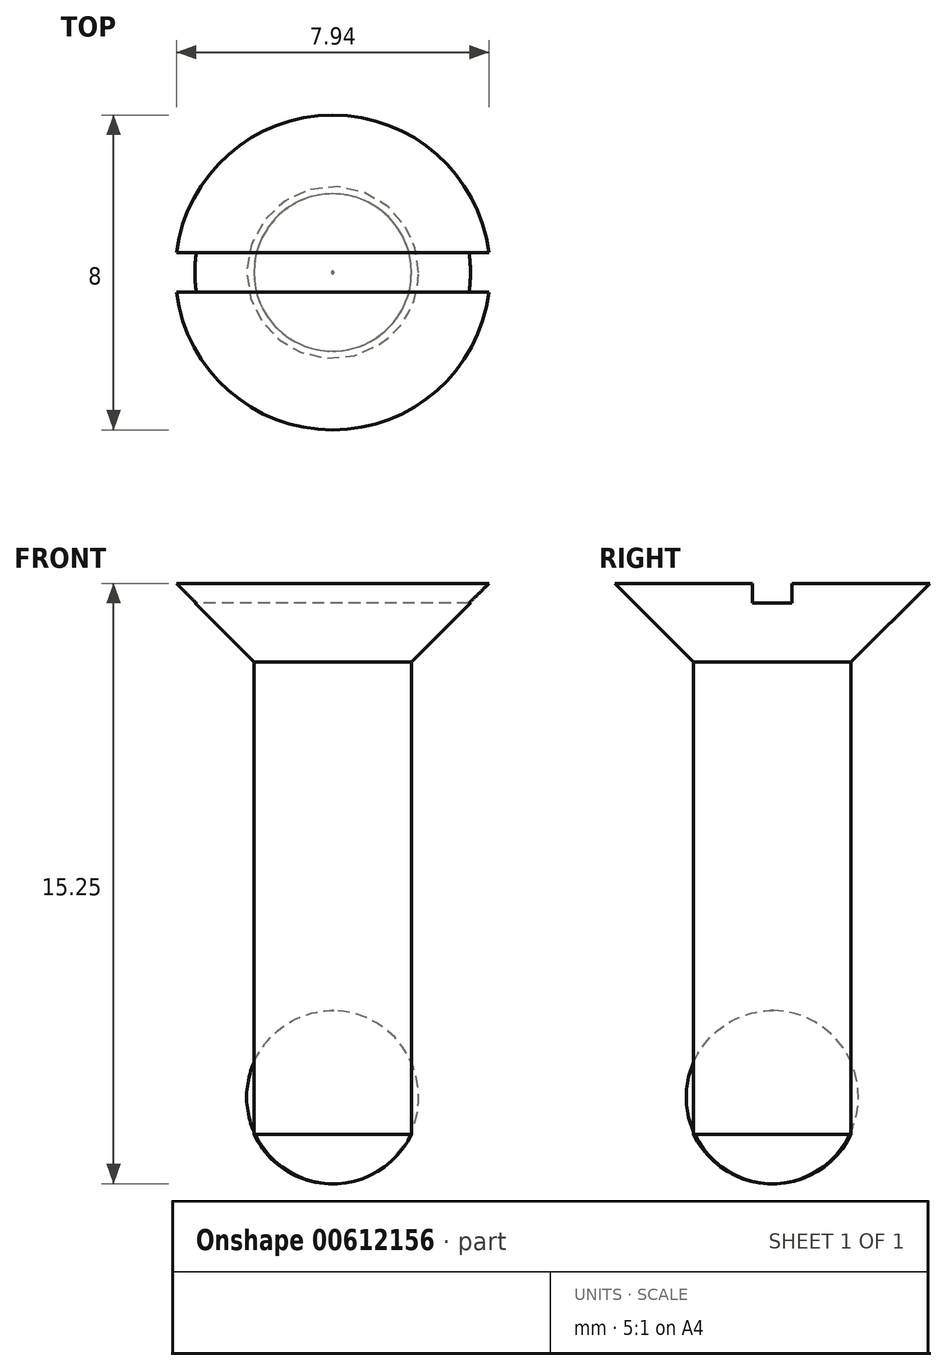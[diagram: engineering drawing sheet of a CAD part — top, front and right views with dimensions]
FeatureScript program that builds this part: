
annotation { "Feature Type Name" : "Feature", "Feature Type Description" : "" }
export const myFeature = defineFeature(function(context is Context, id is Id, definition is map)
    precondition{}
    {
        {
            var Q0;
            Q0=qCreatedBy(makeId("Front.planeOp"),FACE);
            var sketch = newSketch(context, id + "F0", { "sketchPlane" : qUnion([Q0])});
            skLineSegment(sketch, "E0", {"start": v(0, 0) * mm, "end": v(0, 14) * mm});
            skLineSegment(sketch, "E1", {"start": v(0, 14) * mm, "end": v(4, 14) * mm});
            skLineSegment(sketch, "E2", {"start": v(4, 14) * mm, "end": v(2, 12) * mm});
            skLineSegment(sketch, "E3", {"start": v(2, 12) * mm, "end": v(2, 0) * mm});
            skArc(sketch, "E4", {"start": v(0, -1.25) * mm, "mid": v(1.18, -0.92) * mm, "end": v(2, 0) * mm});
            skLineSegment(sketch, "E5", {"start": v(0, -1.25) * mm, "end": v(0, 0) * mm});
            skSolve(sketch);
        }
        {
            var Q0;
            Q0=makeQuery(id+"F0.imprint","IMPRINT",FACE,{"disambiguationData":[TD([[makeQuery(id+"F0.imprint","IMPRINT",EDGE,{"derivedFrom":sQuery(id+"F0.wireOp",EDGE,"E0")}),-1.0]])]});
            var Q1;
            Q1=sQuery(id+"F0.wireOp",EDGE,"E0");
            revolve(context, id + "F1", {"entities" : qUnion([Q0]), "axis" : qUnion([Q1]), "revolveType" : RevolveType.FULL});
        }
        {
            var Q0;
            Q0=makeQuery(id+"F1.opRevolve","SWEPT_FACE",FACE,{"disambiguationData":[OSD([sQuery(id+"F0.wireOp",EDGE,"E1")])]});
            var sketch = newSketch(context, id + "F2", { "sketchPlane" : qUnion([Q0])});
            skLineSegment(sketch, "E6.bottom", {"start": v(5.06, -0.5) * mm, "end": v(-5.06, -0.5) * mm});
            skLineSegment(sketch, "E6.top", {"start": v(5.06, 0.5) * mm, "end": v(-5.06, 0.5) * mm});
            skLineSegment(sketch, "E6.left", {"start": v(5.06, -0.5) * mm, "end": v(5.06, 0.5) * mm});
            skLineSegment(sketch, "E6.right", {"start": v(-5.06, -0.5) * mm, "end": v(-5.06, 0.5) * mm});
            skPoint(sketch, "E6.middle", {"position": v(0, 0) * mm});
            skSolve(sketch);
        }
        {
            var Q0;
            Q0 = qSketchRegion(id + "F2", true);
            extrude(context, id + "F3", {"entities" : qUnion([Q0]), "operationType" : NewBodyOperationType.REMOVE, "oppositeDirection" : true, "depth" : 0.5 * mm, "offsetDistance" : 25 * mm});
        }
    });
